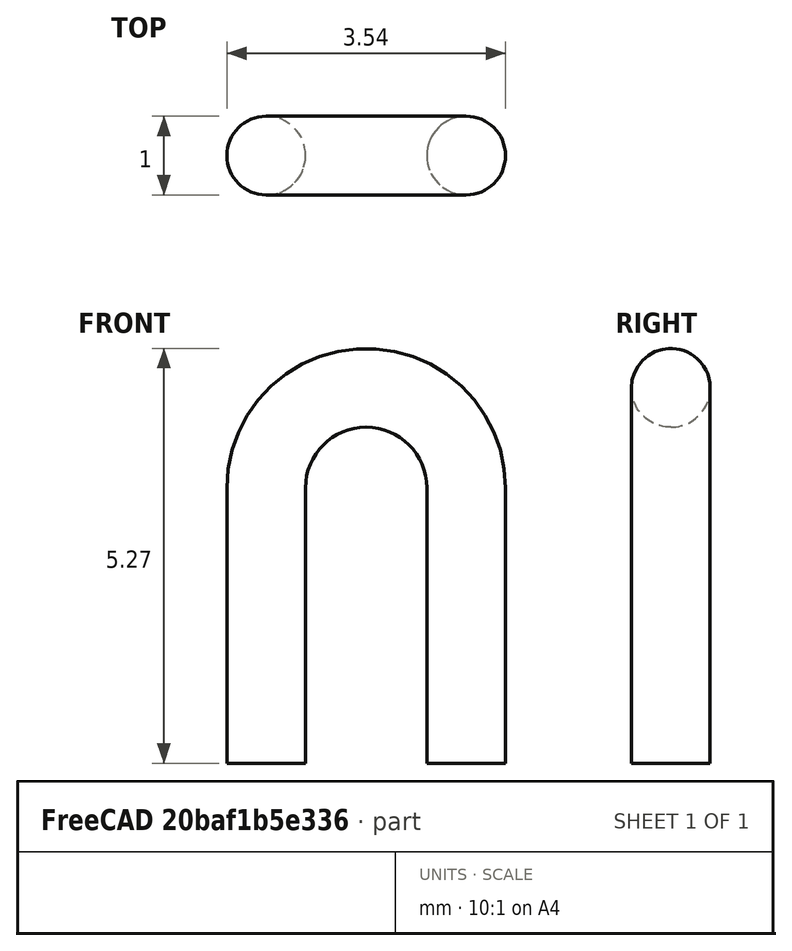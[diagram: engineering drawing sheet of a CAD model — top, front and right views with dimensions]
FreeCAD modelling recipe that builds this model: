
FCSTD DOCUMENT  (FreeCAD 0.17R12018 (Git))
Label: Test_Point_Bridge_Pitch2.54mm_Drill1.3mm
License: All rights reserved
LicenseURL: http://en.wikipedia.org/wiki/All_rights_reserved
objects: Sketcher::SketchObject×2, Spreadsheet::Sheet×1, PartDesign::SubtractivePipe×1, PartDesign::Body×1
note: 5 computed .brp shape members not serialized (recipe doc carries the construction recipe); baked Part::Feature solids carry a one-line shape summary decoded from their .brp

FEATURE [Sketcher::SketchObject] Sketch
  MapMode = 5
  Placement = pos=(0,0,-3) rot=(0,0,1;0rad)
  Support = -> [XY_Plane]
  superPlacement = pos=(0,0,-3) rot=(0,0,1;0rad)
  expr: Constraints[1] = dims.DWire / 2
  sketch-geometry (1):
    g0: Circle CenterX=0 CenterY=0 CenterZ=0 NormalX=0 NormalY=0 NormalZ=1 Radius=0.5
  constraints (2):
    c: Coincident(g0,g-1)
    c: Radius(g0) = 0.5
FEATURE [Spreadsheet::Sheet] Spreadsheet  label="dims"
  cells = A1="DWire"; B1(DWire)=1; A2="Pitch"; B2(Pitch)=2.54
FEATURE [Sketcher::SketchObject] Sketch001
  MapMode = 5
  Placement = pos=(0,0,0) rot=(1,0,0;1.5708rad)
  Support = -> [XZ_Plane]
  expr: Constraints[10] = dims.DWire / 2
  expr: Constraints[3] = dims.Pitch
  sketch-geometry (4):
    g0: LineSegment StartX=0 StartY=-3 StartZ=0 EndX=0 EndY=0.5 EndZ=0
    g1: LineSegment StartX=2.54 StartY=0.5 StartZ=0 EndX=2.54 EndY=-3 EndZ=0
    g2: LineSegment [constr] StartX=0 StartY=0.5 StartZ=0 EndX=2.54 EndY=0.5 EndZ=0
    g3: ArcOfCircle CenterX=1.27 CenterY=0.5 CenterZ=0 NormalX=0 NormalY=0 NormalZ=1 Radius=1.27 StartAngle=0 EndAngle=3.14159
  constraints (13):
    c: PointOnObject(g0,g-2)
    c: Vertical(g0)
    c: Vertical(g1)
    c: DistanceX(g0,g1) = 2.54
    c: Coincident(g2,g0)
    c: Coincident(g2,g1)
    c: Horizontal(g2)
    c: PointOnObject(g3,g2)
    c: Coincident(g3,g0)
    c: Coincident(g3,g1)
    c: DistanceY(g-1,g3) = 0.5
    c: DistanceY(g0,g-1) = 3
    c: Equal(g1,g0)
FEATURE [PartDesign::SubtractivePipe] SubtractivePipe
  AuxilleryCurvelinear = true
  AuxillerySpineTangent = false
  Binormal = (0,0,0)
  Mode = 0
  Profile = -> Sketch
  Spine = -> Sketch001
  SpineTangent = false
  Transformation = 0
  Transition = 0
FEATURE [PartDesign::Body] Body  label="Test_Point_Bridge_Pitch2.54mm_Drill1.3mm"
  Group = -> [Sketch,Sketch001,SubtractivePipe]
  Origin = -> Origin
  Tip = -> SubtractivePipe
